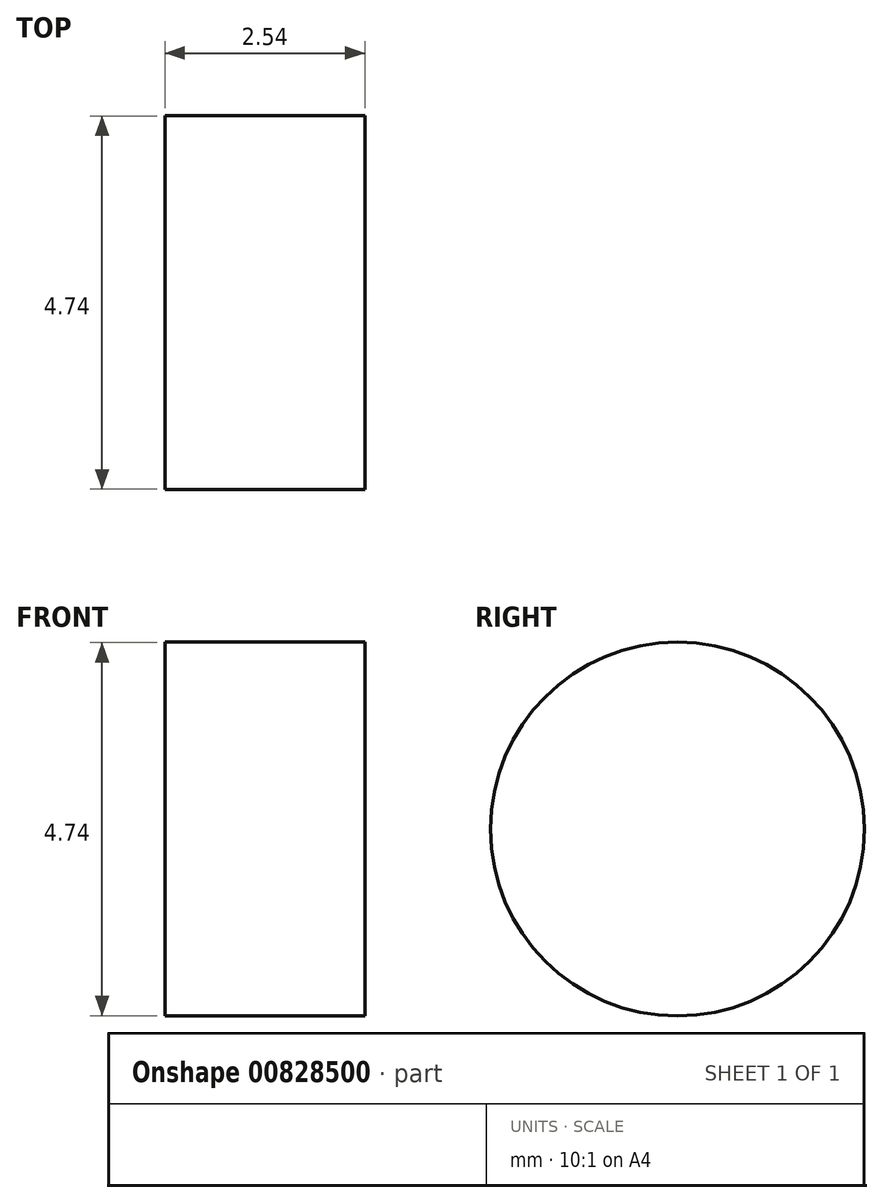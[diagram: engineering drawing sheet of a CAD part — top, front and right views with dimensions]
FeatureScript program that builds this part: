
annotation { "Feature Type Name" : "Feature", "Feature Type Description" : "" }
export const myFeature = defineFeature(function(context is Context, id is Id, definition is map)
    precondition{}
    {
        {
            var Q0;
            Q0=qCreatedBy(makeId("Right.planeOp"),FACE);
            var sketch = newSketch(context, id + "F0", { "sketchPlane" : qUnion([Q0])});
            skCircle(sketch, "E0", {"center": v(0, 0) * mm, "radius": 2.37 * mm});
            skSolve(sketch);
        }
        {
            var Q0;
            Q0 = qSketchRegion(id + "F0", true);
            extrude(context, id + "F1", {"entities" : qUnion([Q0]), "depth" : 2.54 * mm, "offsetDistance" : 25 * mm});
        }
    });
